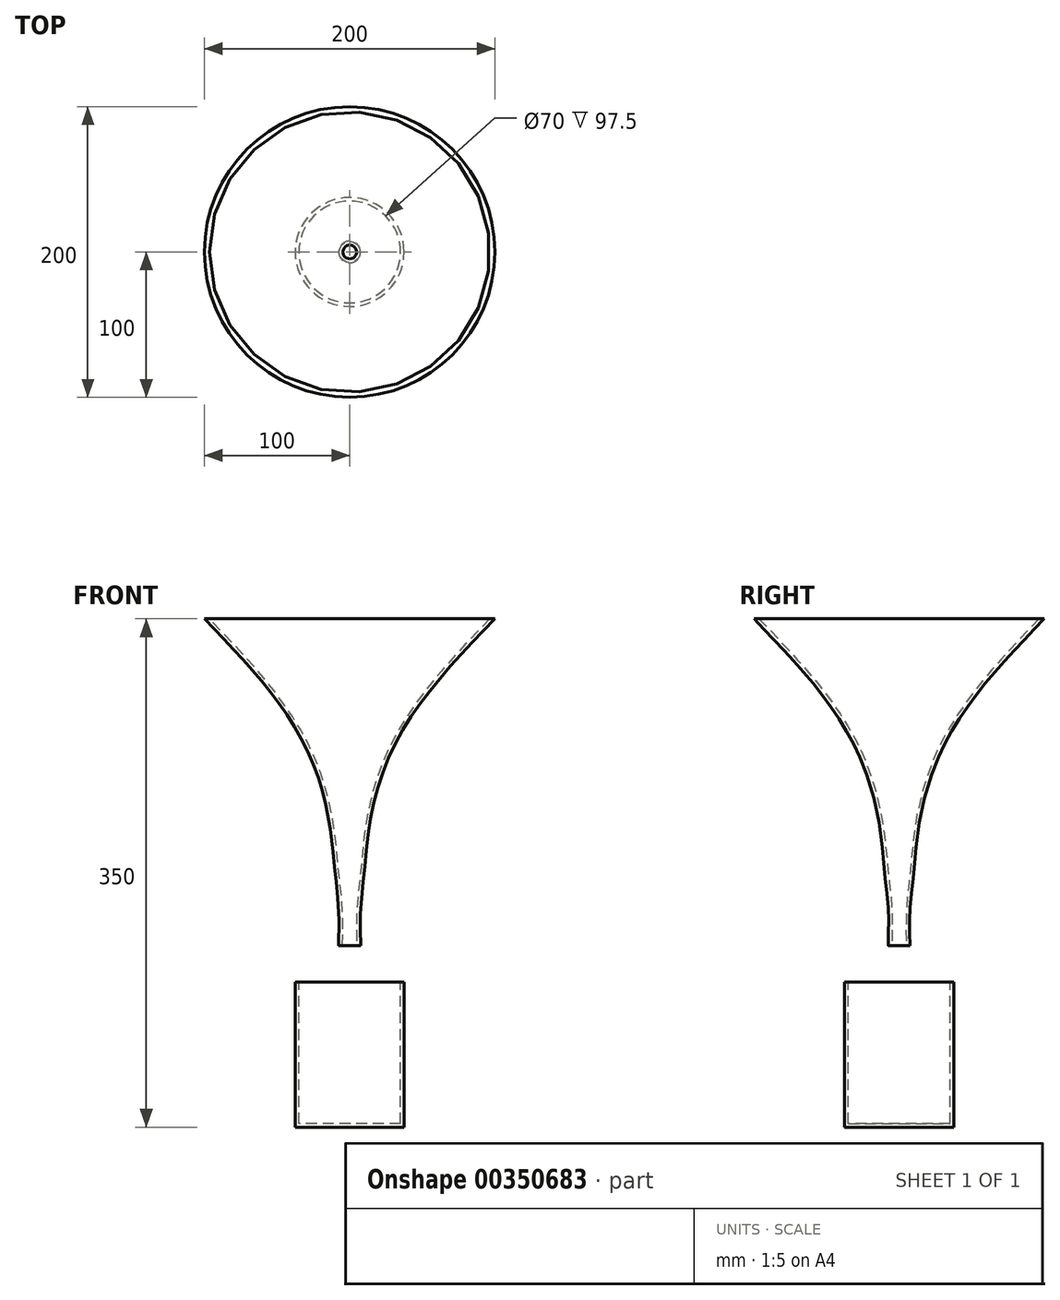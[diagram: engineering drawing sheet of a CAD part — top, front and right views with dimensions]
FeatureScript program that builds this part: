
annotation { "Feature Type Name" : "Feature", "Feature Type Description" : "" }
export const myFeature = defineFeature(function(context is Context, id is Id, definition is map)
    precondition{}
    {
        {
            var Q0;
            Q0=qCreatedBy(makeId("Top.planeOp"),FACE);
            var sketch = newSketch(context, id + "F0", { "sketchPlane" : qUnion([Q0])});
            skCircle(sketch, "E0", {"center": v(0, 0) * mm, "radius": 7.5 * mm});
            skSolve(sketch);
        }
        {
            var Q0;
            Q0=qCreatedBy(makeId("Top.planeOp"),FACE);
            cPlane(context, id + "F1", {"entities" : qUnion([Q0]), "cplaneType" : CPlaneType.OFFSET, "offset" : 25 * mm, "width" : 150 * mm, "height" : 150 * mm});
        }
        {
            var Q0;
            Q0=qCreatedBy(id+"F1.planeOp",FACE);
            var sketch = newSketch(context, id + "F2", { "sketchPlane" : qUnion([Q0])});
            skCircle(sketch, "E1", {"center": v(0, 0) * mm, "radius": 7.5 * mm});
            skSolve(sketch);
        }
        {
            var Q0;
            Q0=qCreatedBy(id+"F1.planeOp",FACE);
            cPlane(context, id + "F3", {"entities" : qUnion([Q0]), "cplaneType" : CPlaneType.OFFSET, "offset" : 25 * mm, "width" : 150 * mm, "height" : 150 * mm});
        }
        {
            var Q0;
            Q0=qCreatedBy(id+"F3.planeOp",FACE);
            var sketch = newSketch(context, id + "F4", { "sketchPlane" : qUnion([Q0])});
            skCircle(sketch, "E2", {"center": v(0, 0) * mm, "radius": 10 * mm});
            skSolve(sketch);
        }
        {
            var Q0;
            Q0=qCreatedBy(id+"F3.planeOp",FACE);
            cPlane(context, id + "F5", {"entities" : qUnion([Q0]), "cplaneType" : CPlaneType.OFFSET, "offset" : 25 * mm, "width" : 150 * mm, "height" : 150 * mm});
        }
        {
            var Q0;
            Q0=qCreatedBy(id+"F5.planeOp",FACE);
            var sketch = newSketch(context, id + "F6", { "sketchPlane" : qUnion([Q0])});
            skCircle(sketch, "E3", {"center": v(0, 0) * mm, "radius": 12.5 * mm});
            skSolve(sketch);
        }
        {
            var Q0;
            Q0=qCreatedBy(id+"F5.planeOp",FACE);
            cPlane(context, id + "F7", {"entities" : qUnion([Q0]), "cplaneType" : CPlaneType.OFFSET, "offset" : 50 * mm, "width" : 150 * mm, "height" : 150 * mm});
        }
        {
            var Q0;
            Q0=qCreatedBy(id+"F7.planeOp",FACE);
            var sketch = newSketch(context, id + "F8", { "sketchPlane" : qUnion([Q0])});
            skCircle(sketch, "E4", {"center": v(0, 0) * mm, "radius": 25 * mm});
            skSolve(sketch);
        }
        {
            var Q0;
            Q0=qCreatedBy(id+"F7.planeOp",FACE);
            cPlane(context, id + "F9", {"entities" : qUnion([Q0]), "cplaneType" : CPlaneType.OFFSET, "offset" : 100 * mm, "width" : 150 * mm, "height" : 150 * mm});
        }
        {
            var Q0;
            Q0=qCreatedBy(id+"F9.planeOp",FACE);
            var sketch = newSketch(context, id + "F10", { "sketchPlane" : qUnion([Q0])});
            skCircle(sketch, "E5", {"center": v(0, 0) * mm, "radius": 100 * mm});
            skSolve(sketch);
        }
        {
            var Q0;
            Q0=makeQuery(id+"F0.imprint","IMPRINT",FACE,{"disambiguationData":[TD([[makeQuery(id+"F0.imprint","IMPRINT",EDGE,{"derivedFrom":sQuery(id+"F0.wireOp",EDGE,"E0")}),1.0]])]});
            var Q1;
            Q1=makeQuery(id+"F2.imprint","IMPRINT",FACE,{"disambiguationData":[TD([[makeQuery(id+"F2.imprint","IMPRINT",EDGE,{"derivedFrom":sQuery(id+"F2.wireOp",EDGE,"E1")}),1.0]])]});
            var Q2;
            Q2=makeQuery(id+"F4.imprint","IMPRINT",FACE,{"disambiguationData":[TD([[makeQuery(id+"F4.imprint","IMPRINT",EDGE,{"derivedFrom":sQuery(id+"F4.wireOp",EDGE,"E2")}),1.0]])]});
            var Q3;
            Q3=makeQuery(id+"F6.imprint","IMPRINT",FACE,{"disambiguationData":[TD([[makeQuery(id+"F6.imprint","IMPRINT",EDGE,{"derivedFrom":sQuery(id+"F6.wireOp",EDGE,"E3")}),1.0]])]});
            var Q4;
            Q4=makeQuery(id+"F8.imprint","IMPRINT",FACE,{"disambiguationData":[TD([[makeQuery(id+"F8.imprint","IMPRINT",EDGE,{"derivedFrom":sQuery(id+"F8.wireOp",EDGE,"E4")}),1.0]])]});
            var Q5;
            Q5=makeQuery(id+"F10.imprint","IMPRINT",FACE,{"disambiguationData":[TD([[makeQuery(id+"F10.imprint","IMPRINT",EDGE,{"derivedFrom":sQuery(id+"F10.wireOp",EDGE,"E5")}),1.0]])]});
            loft(context, id + "F11", {"sheetProfilesArray" : [{ "sheetProfileEntities" : qUnion([Q0]) }, { "sheetProfileEntities" : qUnion([Q1]) }, { "sheetProfileEntities" : qUnion([Q2]) }, { "sheetProfileEntities" : qUnion([Q3]) }, { "sheetProfileEntities" : qUnion([Q4]) }, { "sheetProfileEntities" : qUnion([Q5]) }]});
        }
        {
            var Q0;
            Q0=makeQuery(id+"F11.opLoft","CAP_FACE",FACE,{"disambiguationData":[OSD([makeQuery(id+"F10.imprint","IMPRINT",FACE,{"disambiguationData":[TD([[makeQuery(id+"F10.imprint","IMPRINT",EDGE,{"derivedFrom":sQuery(id+"F10.wireOp",EDGE,"E5")}),1.0]])]})])],"isStart":true});
            var Q1;
            Q1=makeQuery(id+"F11.opLoft","CAP_FACE",FACE,{"disambiguationData":[OSD([makeQuery(id+"F0.imprint","IMPRINT",FACE,{"disambiguationData":[TD([[makeQuery(id+"F0.imprint","IMPRINT",EDGE,{"derivedFrom":sQuery(id+"F0.wireOp",EDGE,"E0")}),1.0]])]})])],"isStart":true});
            shell(context, id + "F12", {"entities" : qUnion([Q0, Q1]), "thickness" : 2.5 * mm});
        }
        {
            var Q0;
            Q0=qCreatedBy(makeId("Top.planeOp"),FACE);
            cPlane(context, id + "F13", {"entities" : qUnion([Q0]), "cplaneType" : CPlaneType.OFFSET, "offset" : 25 * mm, "oppositeDirection" : true, "width" : 150 * mm, "height" : 150 * mm});
        }
        {
            var Q0;
            Q0=qCreatedBy(id+"F13.planeOp",FACE);
            var sketch = newSketch(context, id + "F14", { "sketchPlane" : qUnion([Q0])});
            skCircle(sketch, "E6", {"center": v(0, 0) * mm, "radius": 37.5 * mm});
            skSolve(sketch);
        }
        {
            var Q0;
            Q0=makeQuery(id+"F14.imprint","IMPRINT",FACE,{"disambiguationData":[TD([[makeQuery(id+"F14.imprint","IMPRINT",EDGE,{"derivedFrom":sQuery(id+"F14.wireOp",EDGE,"E6")}),1.0]])]});
            extrude(context, id + "F15", {"entities" : qUnion([Q0]), "oppositeDirection" : true, "depth" : 100 * mm});
        }
        {
            var Q0;
            Q0=makeQuery(id+"F15.opExtrude","CAP_FACE",FACE,{"disambiguationData":[OSD([sQuery(id+"F14.wireOp",EDGE,"E6")])],"isStart":true});
            shell(context, id + "F16", {"entities" : qUnion([Q0]), "thickness" : 2.5 * mm});
        }
    });
